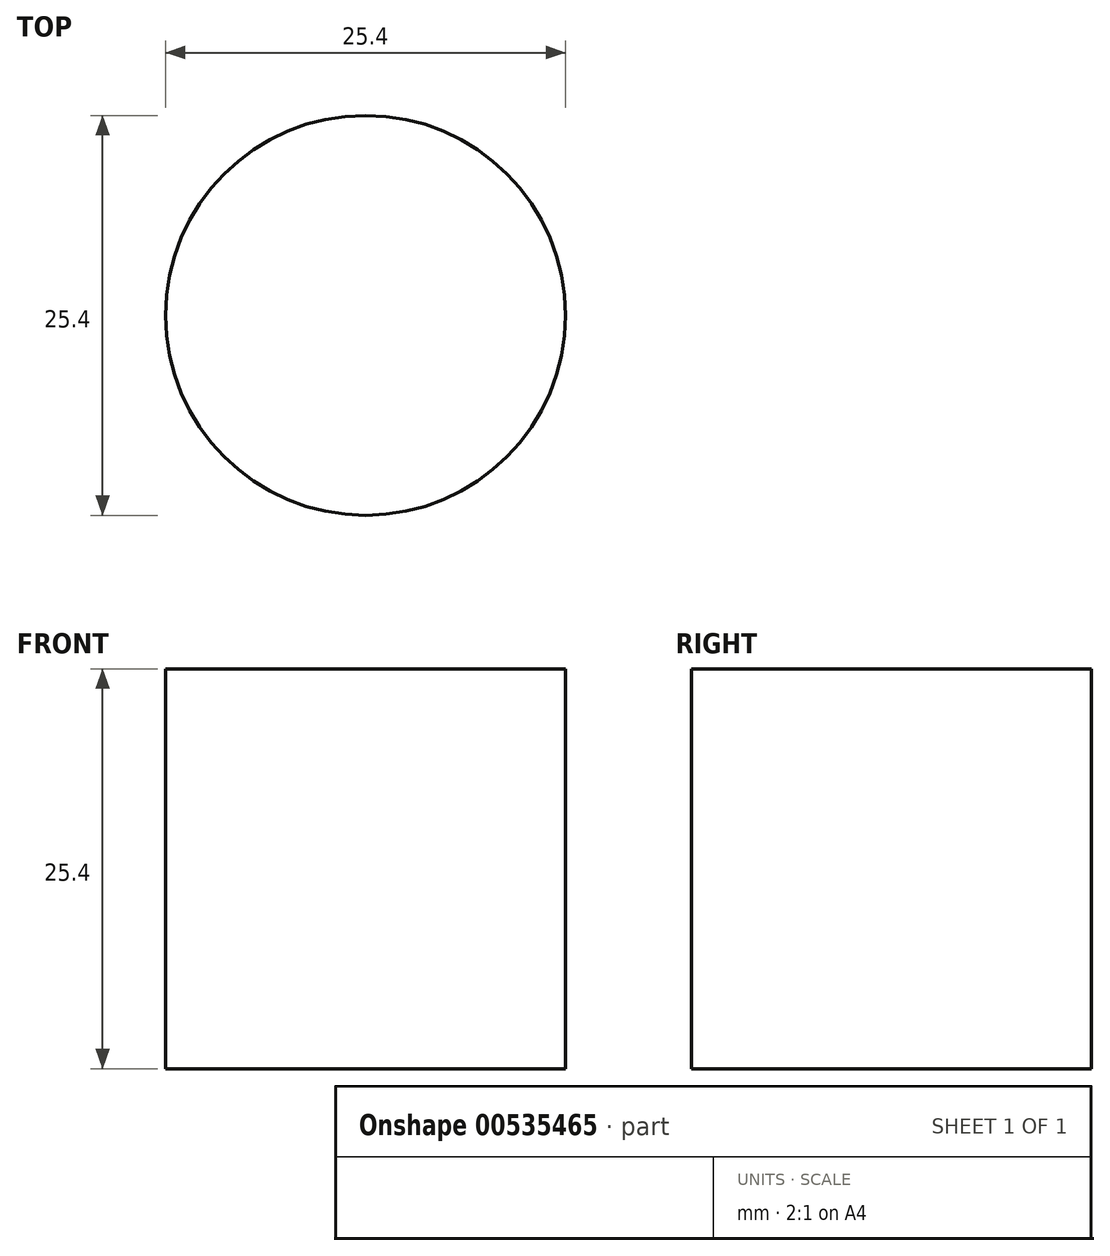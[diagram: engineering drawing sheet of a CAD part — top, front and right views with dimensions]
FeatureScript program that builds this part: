
annotation { "Feature Type Name" : "Feature", "Feature Type Description" : "" }
export const myFeature = defineFeature(function(context is Context, id is Id, definition is map)
    precondition{}
    {
        {
            var Q0;
            Q0=qCreatedBy(makeId("Top.planeOp"),FACE);
            var sketch = newSketch(context, id + "F0", { "sketchPlane" : qUnion([Q0])});
            skCircle(sketch, "E0", {"center": v(0, 0) * mm, "radius": 12.7 * mm});
            skSolve(sketch);
        }
        {
            var Q0;
            Q0=makeQuery(id+"F0.imprint","IMPRINT",FACE,{"disambiguationData":[TD([[makeQuery(id+"F0.imprint","IMPRINT",EDGE,{"derivedFrom":sQuery(id+"F0.wireOp",EDGE,"E0")}),1.0]])]});
            extrude(context, id + "F1", {"entities" : qUnion([Q0]), "oppositeDirection" : true, "depth" : 25.4 * mm, "offsetDistance" : 25.4 * mm});
        }
        {
            var Q0;
            Q0=qCreatedBy(makeId("Top.planeOp"),FACE);
            cPlane(context, id + "F2", {"entities" : qUnion([Q0]), "cplaneType" : CPlaneType.OFFSET, "offset" : 38.1 * mm, "oppositeDirection" : true, "width" : 152.4 * mm, "height" : 152.4 * mm});
        }
        {
            var Q0;
            Q0=qCreatedBy(makeId("Front.planeOp"),FACE);
            var sketch = newSketch(context, id + "F3", { "sketchPlane" : qUnion([Q0])});
            skArc(sketch, "E1", {"start": v(-12.7, -25.38) * mm, "mid": v(-8.99, -34.37) * mm, "end": v(0, -38.1) * mm});
            skLineSegment(sketch, "E2", {"start": v(0, -38.1) * mm, "end": v(0, -25.4) * mm, "construction": true});
            skSolve(sketch);
        }
        {
            var Q0;
            Q0=sQuery(id+"F3.wireOp",EDGE,"E1");
            var Q1;
            Q1=sQuery(id+"F3.wireOp",EDGE,"E2");
            revolve(context, id + "F4", {"bodyType" : ToolBodyType.SURFACE, "surfaceEntities" : qUnion([Q0]), "axis" : qUnion([Q1]), "revolveType" : RevolveType.FULL});
        }
    });
